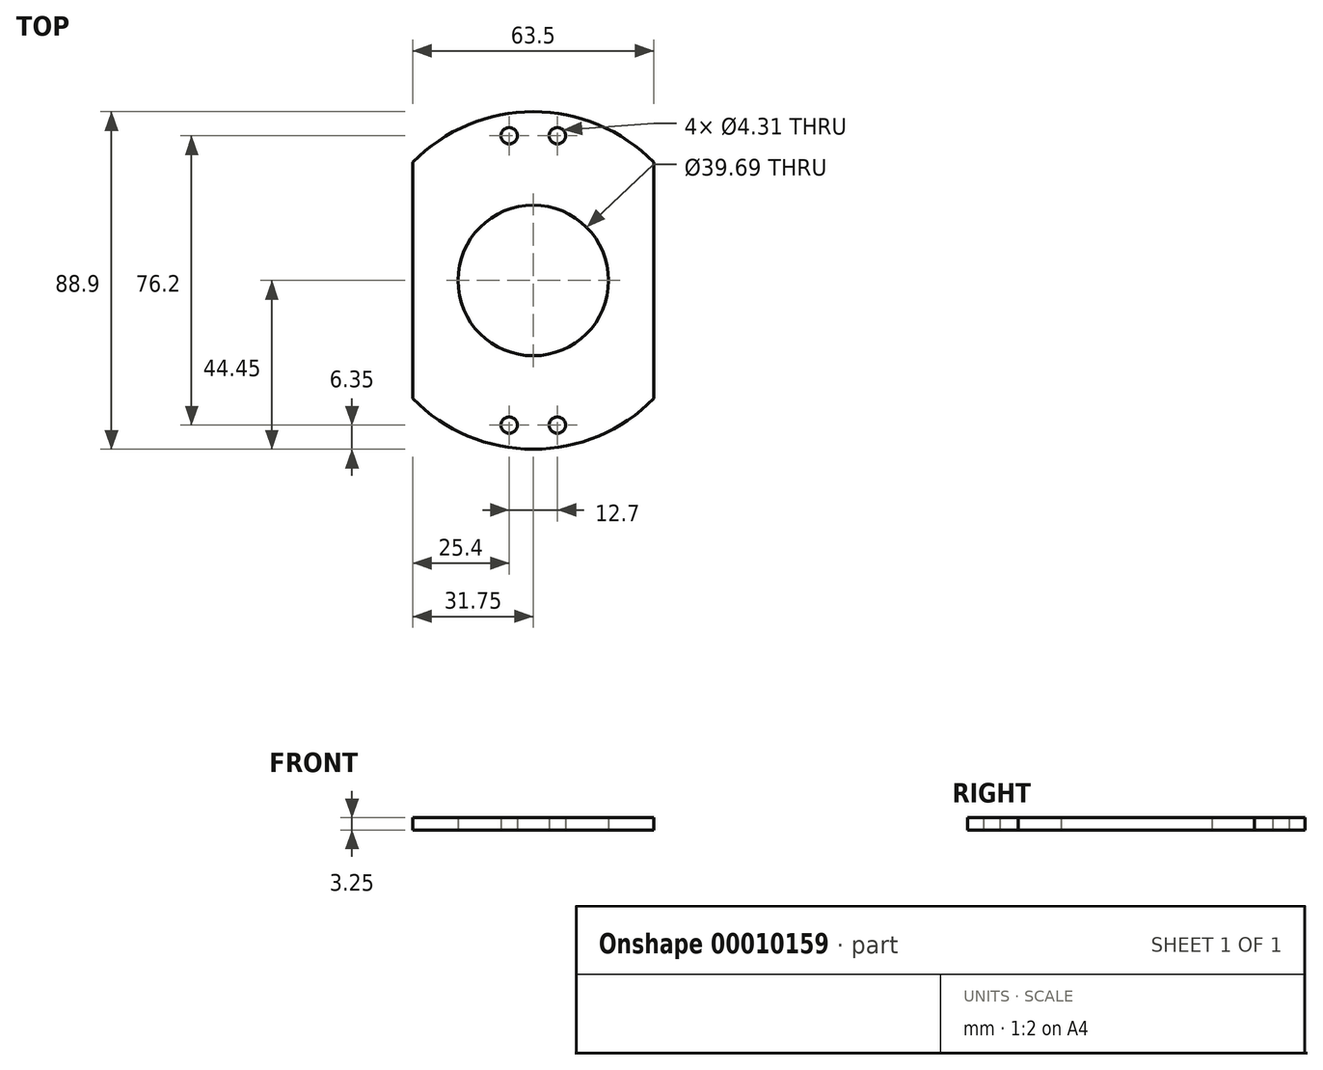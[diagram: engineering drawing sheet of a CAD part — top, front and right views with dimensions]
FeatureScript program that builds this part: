
annotation { "Feature Type Name" : "Feature", "Feature Type Description" : "" }
export const myFeature = defineFeature(function(context is Context, id is Id, definition is map)
    precondition{}
    {
        {
            var Q0;
            Q0=qCreatedBy(makeId("Top.planeOp"),FACE);
            var sketch = newSketch(context, id + "F0", { "sketchPlane" : qUnion([Q0])});
            skCircle(sketch, "E0", {"center": v(0, 0) * mm, "radius": 19.84 * mm});
            skArc(sketch, "E1", {"start": v(-31.75, -31.1) * mm, "mid": v(0, -44.45) * mm, "end": v(31.75, -31.1) * mm});
            skLineSegment(sketch, "E2", {"start": v(-31.75, 31.1) * mm, "end": v(-31.75, -31.1) * mm});
            skLineSegment(sketch, "E3", {"start": v(31.75, 31.1) * mm, "end": v(31.75, -31.1) * mm});
            skArc(sketch, "E4.trimOffspring", {"start": v(31.75, 31.1) * mm, "mid": v(0, 44.45) * mm, "end": v(-31.75, 31.1) * mm});
            skSolve(sketch);
        }
        {
            var Q0;
            Q0 = qSketchRegion(id + "F0", true);
            extrude(context, id + "F1", {"entities" : qUnion([Q0]), "depth" : 3.25 * mm});
        }
        {
            var Q0;
            Q0=makeQuery(id+"F1.opExtrude","CAP_FACE",FACE,{"disambiguationData":[OSD([sQuery(id+"F0.wireOp",EDGE,"E0"),sQuery(id+"F0.wireOp",EDGE,"E1")])],"isStart":true});
            var sketch = newSketch(context, id + "F2", { "sketchPlane" : qUnion([Q0])});
            skLineSegment(sketch, "E5", {"start": v(-22.9, -38.1) * mm, "end": v(22.9, -38.1) * mm, "construction": true});
            skCircle(sketch, "E6", {"center": v(-6.35, -38.1) * mm, "radius": 2.15 * mm});
            skLineSegment(sketch, "E7", {"start": v(0, -44.45) * mm, "end": v(0, 0) * mm, "construction": true});
            skCircle(sketch, "E8.0.MirrorC", {"center": v(6.35, -38.1) * mm, "radius": 2.15 * mm});
            skLineSegment(sketch, "E9", {"start": v(-44.45, 0) * mm, "end": v(44.45, 0) * mm, "construction": true});
            skCircle(sketch, "E10.0.MirrorC", {"center": v(6.35, 38.1) * mm, "radius": 2.15 * mm});
            skCircle(sketch, "E11.0.MirrorC", {"center": v(-6.35, 38.1) * mm, "radius": 2.15 * mm});
            skSolve(sketch);
        }
        {
            var Q0;
            Q0 = qSketchRegion(id + "F2", true);
            extrude(context, id + "F3", {"entities" : qUnion([Q0]), "operationType" : NewBodyOperationType.REMOVE, "endBound" : BoundingType.UP_TO_NEXT, "oppositeDirection" : true, "depth" : 25.4 * mm});
        }
    });
